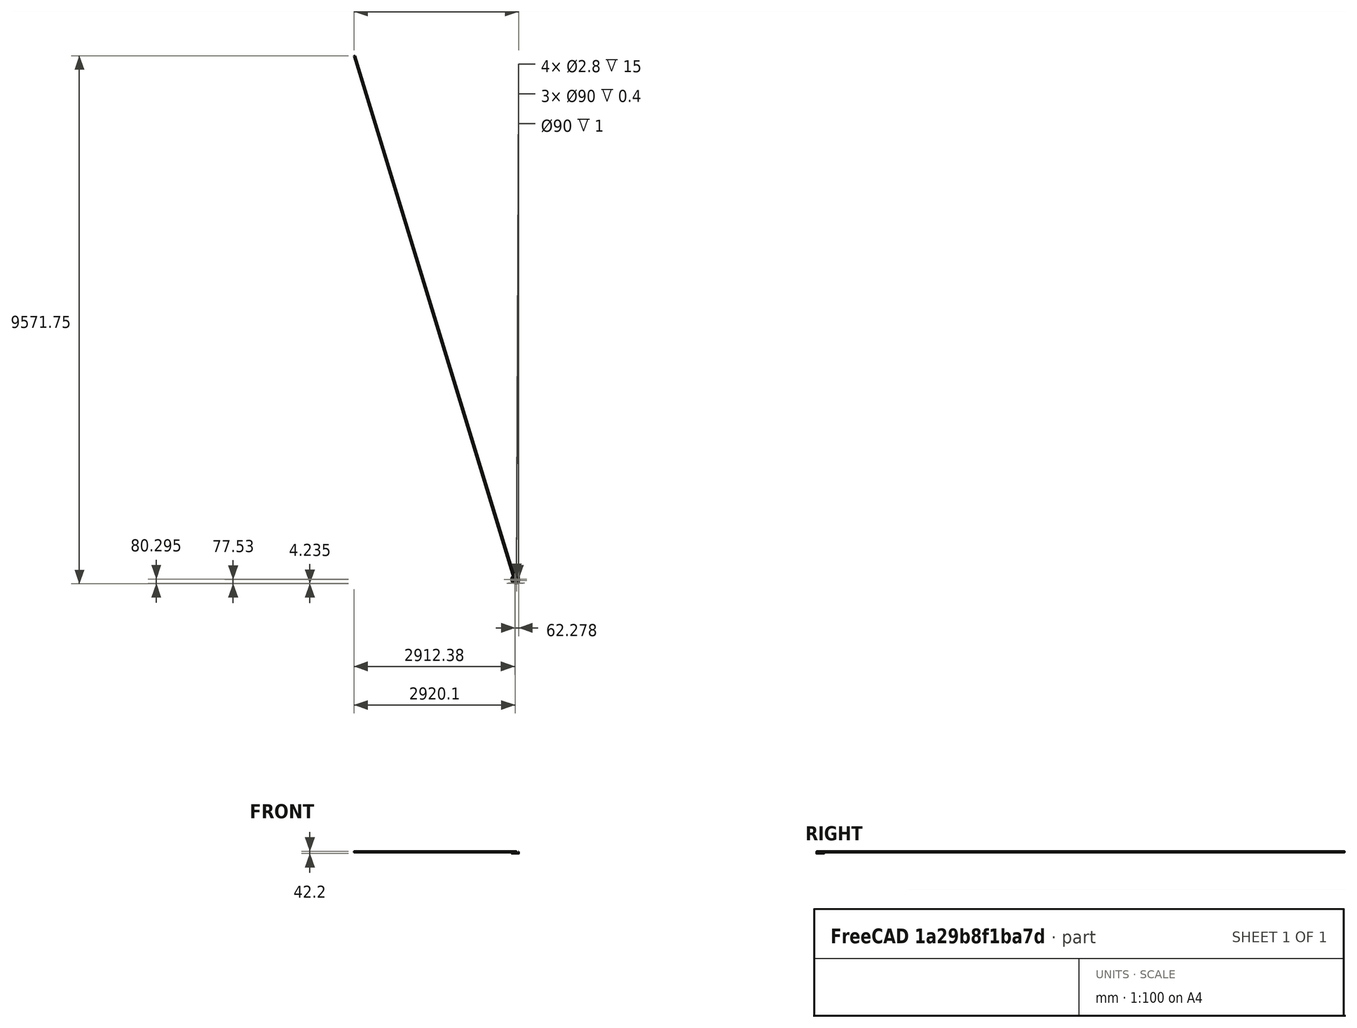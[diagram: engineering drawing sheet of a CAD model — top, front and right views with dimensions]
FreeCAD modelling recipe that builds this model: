
FCSTD DOCUMENT  (FreeCAD 0.16R)
Label: chainguard25TRev1.V5
License: All rights reserved
LicenseURL: http://en.wikipedia.org/wiki/All_rights_reserved
objects: Sketcher::SketchObject×9, PartDesign::Fillet×9, PartDesign::Pad×5, PartDesign::Pocket×4, Part::FeaturePython×3, Mesh::Feature×3
note: 39 computed .brp shape members not serialized (recipe doc carries the construction recipe); baked Part::Feature solids carry a one-line shape summary decoded from their .brp

FEATURE [Sketcher::SketchObject] Sketch001
  sketch-geometry (7):
    g0: LineSegment StartX=60 StartY=64 StartZ=0 EndX=0 EndY=64 EndZ=0
    g1: LineSegment StartX=60 StartY=-64 StartZ=0 EndX=0 EndY=-64 EndZ=0
    g2: ArcOfCircle CenterX=8.21903e-05 CenterY=0 CenterZ=0 NormalX=0 NormalY=0 NormalZ=1 Radius=64 StartAngle=1.5708 EndAngle=4.71239
    g3: Circle CenterX=0 CenterY=0 CenterZ=0 NormalX=0 NormalY=0 NormalZ=1 Radius=45
    g4: ArcOfCircle CenterX=60 CenterY=51 CenterZ=0 NormalX=0 NormalY=0 NormalZ=1 Radius=13 StartAngle=0 EndAngle=1.5708
    g5: ArcOfCircle CenterX=60 CenterY=-51 CenterZ=0 NormalX=0 NormalY=0 NormalZ=1 Radius=13 StartAngle=4.71239 EndAngle=6.28319
    g6: LineSegment StartX=73 StartY=51 StartZ=0 EndX=73 EndY=-51 EndZ=0
  constraints (23):
    c: Horizontal(g0)
    c: Horizontal(g1)
    c: Coincident(g2,g1)
    c: Coincident(g0,g2)
    c: DistanceX(g1,g0) = 0
    c: Equal(g0,g1)
    c: DistanceY(g1,g0) = 128
    c: Radius(g2) = 64
    c: Symmetric(g1,g0,g-1)
    c: Radius(g3) = 45
    c: Coincident(g3,g-1)
    c: PointOnObject(g4,g0)
    c: Radius(g4) = 13
    c: DistanceX(g0,g0) = 60
    c: Equal(g5,g4)
    c: Vertical(g6)
    c: DistanceX(g-1,g6) = 73
    c: Symmetric(g6,g6,g-1)
    c: DistanceY(g6,g6) = 102
    c: Coincident(g4,g6)
    c: Coincident(g5,g6)
    c: Coincident(g1,g5)
    c: Coincident(g0,g4)
FEATURE [PartDesign::Pad] Pad  label="Faceplate"
  Length = 1
  Length2 = 100
  Reversed = true
  Sketch = -> Sketch001
  Type = 0
FEATURE [Sketcher::SketchObject] Sketch002
  sketch-geometry (8):
    g0: LineSegment StartX=60 StartY=64 StartZ=0 EndX=0 EndY=64 EndZ=0
    g1: LineSegment StartX=60 StartY=-64 StartZ=0 EndX=0 EndY=-64 EndZ=0
    g2: ArcOfCircle CenterX=6.44712e-05 CenterY=0 CenterZ=0 NormalX=0 NormalY=0 NormalZ=1 Radius=64 StartAngle=1.5708 EndAngle=4.71239
    g3: LineSegment StartX=0 StartY=62 StartZ=0 EndX=60 EndY=62 EndZ=0
    g4: LineSegment StartX=0 StartY=-62 StartZ=0 EndX=60 EndY=-62 EndZ=0
    g5: LineSegment StartX=60 StartY=64 StartZ=0 EndX=60 EndY=62 EndZ=0
    g6: LineSegment StartX=60 StartY=-62 StartZ=0 EndX=60 EndY=-64 EndZ=0
    g7: ArcOfCircle CenterX=1.45954e-05 CenterY=0 CenterZ=0 NormalX=0 NormalY=0 NormalZ=1 Radius=62 StartAngle=1.5708 EndAngle=4.71239
  constraints (25):
    c: Horizontal(g0)
    c: Horizontal(g1)
    c: Coincident(g2,g1)
    c: Coincident(g0,g2)
    c: DistanceX(g1,g0) = 0
    c: Equal(g0,g1)
    c: DistanceY(g1,g0) = 128
    c: Radius(g2) = 64
    c: Symmetric(g1,g0,g-1)
    c: Radius(g7) = 62
    c: Parallel(g0,g3)
    c: DistanceY(g3,g0) = 2
    c: DistanceY(g1,g4) = 2
    c: Parallel(g4,g1)
    c: DistanceX(g0,g3) = 0
    c: DistanceX(g4) = 0
    c: DistanceX(g0) = 60
    c: Equal(g3,g0)
    c: Equal(g4,g0)
    c: Coincident(g4,g6)
    c: Coincident(g6,g1)
    c: Coincident(g5,g3)
    c: Coincident(g5,g0)
    c: Coincident(g7,g3)
    c: Coincident(g7,g4)
FEATURE [PartDesign::Pad] Pad001  label="Connector"
  Length = 10
  Length2 = 100
  Sketch = -> Sketch002
  Type = 0
FEATURE [Sketcher::SketchObject] Sketch004  label="BossST"
  sketch-geometry (5):
    g0: LineSegment StartX=41.8431 StartY=-62 StartZ=0 EndX=1.8431 EndY=-62 EndZ=0
    g1: LineSegment StartX=1.8431 StartY=-62 StartZ=0 EndX=1.8431 EndY=-75.5264 EndZ=0
    g2: LineSegment StartX=41.8431 StartY=-66 StartZ=0 EndX=41.8431 EndY=-62 EndZ=0
    g3: LineSegment StartX=4.42784 StartY=-77.439 StartZ=0 EndX=41.8431 EndY=-66 EndZ=0
    g4: ArcOfCircle CenterX=3.8431 CenterY=-75.5264 CenterZ=0 NormalX=0 NormalY=0 NormalZ=1 Radius=2 StartAngle=3.14159 EndAngle=5.00909
  constraints (14):
    c: Coincident(g0,g1)
    c: Vertical(g1)
    c: Vertical(g2)
    c: DistanceX(g0,g0) = 40
    c: Angle(g3) = 0.296706
    c: DistanceY(g0,g-1) = 62
    c: Horizontal(g0)
    c: DistanceY(g2,g2) = 4
    c: Coincident(g2,g0)
    c: Coincident(g3,g2)
    c: Tangent(g3,g4) = -1.5708
    c: Tangent(g1,g4) = -1.5708
    c: Radius(g4) = 2
    c: DistanceX(g-1,g0) = 1.8431
FEATURE [Sketcher::SketchObject] Sketch
  Support = -> Pad [Face8]
  sketch-geometry (4):
    g0: LineSegment StartX=65 StartY=35 StartZ=0 EndX=73 EndY=35 EndZ=0
    g1: LineSegment StartX=73 StartY=35 StartZ=0 EndX=73 EndY=-35 EndZ=0
    g2: LineSegment StartX=73 StartY=-35 StartZ=0 EndX=65 EndY=-35 EndZ=0
    g3: LineSegment StartX=65 StartY=-35 StartZ=0 EndX=65 EndY=35 EndZ=0
  constraints (12):
    c: Coincident(g0,g1)
    c: Coincident(g1,g2)
    c: Coincident(g2,g3)
    c: Coincident(g3,g0)
    c: Horizontal(g0)
    c: Horizontal(g2)
    c: Vertical(g1)
    c: Vertical(g3)
    c: Symmetric(g0,g2,g-1)
    c: DistanceX(g0,g0) = 8
    c: DistanceX(g-1,g0) = 73
    c: DistanceY(g3,g3) = 70
FEATURE [PartDesign::Pad] Pad003  label="SyncStiffener"
  Length = 3
  Length2 = 100
  Sketch = -> Sketch
  Type = 0
FEATURE [PartDesign::Pad] Pad005  label="ST Boss"
  Length = 31
  Length2 = 1
  Sketch = -> Sketch004
  Type = 4
FEATURE [Sketcher::SketchObject] Sketch005
  Placement = pos=(22.0436,-72.1013,0) rot=(0.978386,0.146221,0.146221;1.59265rad)
  Support = -> Pad005 [Face3]
  sketch-geometry (1):
    g0: Circle CenterX=0 CenterY=30 CenterZ=0 NormalX=0 NormalY=0 NormalZ=1 Radius=11.2
  constraints (3):
    c: Radius(g0) = 11.2
    c: DistanceY(g-1,g0) = 30
    c: PointOnObject(g0,g-2)
FEATURE [PartDesign::Pocket] Pocket  label="STHolePocket"
  Length = 5
  Sketch = -> Sketch005
  Type = 1
FEATURE [Sketcher::SketchObject] Sketch007
  Placement = pos=(0,0,31) rot=(0,0,1;0rad)
  Support = -> Pocket [Face4]
  sketch-geometry (4):
    g0: LineSegment StartX=-4.66376 StartY=-53.9533 StartZ=0 EndX=-5.90948 EndY=-71.4649 EndZ=0
    g1: LineSegment StartX=-5.90948 StartY=-71.4649 StartZ=0 EndX=38.1328 EndY=-58 EndZ=0
    g2: LineSegment StartX=38.1328 StartY=-58 StartZ=0 EndX=37.116 EndY=-54.0061 EndZ=0
    g3: LineSegment StartX=37.116 StartY=-54.0061 StartZ=0 EndX=-4.66376 EndY=-53.9533 EndZ=0
  constraints (12):
    c: Coincident(g0,g1)
    c: Coincident(g1,g2)
    c: Coincident(g2,g3)
    c: Coincident(g0,g3)
    c: Distance(g3) = 41.7798
    c: Distance(g0) = 17.5559
    c: Distance(g1) = 46.0546
    c: Distance(g2) = 4.12132
    c: DistanceX(g0,g-1) = 4.66376
    c: DistanceX(g0,g-1) = 5.90948
    c: DistanceY(g2,g-1) = 54.0061
    c: DistanceX(g1) = 38.1328
FEATURE [PartDesign::Pocket] Pocket006  label="STpocket1"
  Length = 22
  Sketch = -> Sketch007
  Type = 0
FEATURE [PartDesign::Fillet] Fillet  label="FaceFillet"
  Base = -> Pad003 [Edge4,Edge12,Edge20,Edge21,Edge22,Edge6,Edge23]
  Radius = 0.6
FEATURE [Sketcher::SketchObject] Sketch014
  ExternalGeometry = -> [Fillet]
  Placement = pos=(73,0,0) rot=(0.57735,0.57735,0.57735;2.0944rad)
  Support = -> Fillet [Face8]
  sketch-geometry (6):
    g0: LineSegment StartX=-35 StartY=3 StartZ=0 EndX=-24.5 EndY=31 EndZ=0
    g1: LineSegment StartX=-24.5 StartY=31 StartZ=0 EndX=-18.2 EndY=31 EndZ=0
    g2: LineSegment StartX=10.5 StartY=31 StartZ=0 EndX=35 EndY=3 EndZ=0
    g3: LineSegment StartX=35 StartY=3 StartZ=0 EndX=-35 EndY=3 EndZ=0
    g4: ArcOfCircle CenterX=-7 CenterY=31 CenterZ=0 NormalX=0 NormalY=0 NormalZ=1 Radius=11.2 StartAngle=3.14159 EndAngle=6.28319
    g5: LineSegment StartX=4.2 StartY=31 StartZ=0 EndX=10.5 EndY=31 EndZ=0
  constraints (16):
    c: Coincident(g0,g1)
    c: Coincident(g0,g3)
    c: Coincident(g1,g4)
    c: Coincident(g2,g3)
    c: Coincident(g2,g5)
    c: Coincident(g4,g5)
    c: Coincident(g0,g-4)
    c: Coincident(g-4,g2)
    c: DistanceX(g-1,g2) = 10.5
    c: DistanceY(g-1,g4) = 31
    c: Radius(g4) = 11.2
    c: DistanceX(g0,g2) = 35
    c: Symmetric(g2,g0,g4)
    c: Horizontal(g1)
    c: Horizontal(g5)
    c: DistanceY(g-1,g4) = 31
FEATURE [PartDesign::Pad] Pad006
  Length = 6
  Length2 = 100
  Reversed = true
  Sketch = -> Sketch014
  Type = 0
FEATURE [Sketcher::SketchObject] Sketch015
  ExternalGeometry = -> [Pad006]
  Placement = pos=(0,0,31) rot=(0,0,1;0rad)
  Support = -> Pad006 [Face7]
  sketch-geometry (2):
    g0: Circle CenterX=70 CenterY=7 CenterZ=0 NormalX=0 NormalY=0 NormalZ=1 Radius=1.4
    g1: Circle CenterX=70 CenterY=-21 CenterZ=0 NormalX=0 NormalY=0 NormalZ=1 Radius=1.4
  constraints (6):
    c: Radius(g1) = 1.4
    c: Equal(g1,g0)
    c: Distance(g1,g0) = 28
    c: Distance(g0,g-3) = 2.8
    c: Distance(g1,g-6) = 3
    c: Distance(g0,g-4) = 3
FEATURE [PartDesign::Pocket] Pocket008  label="SyncHoles"
  Length = 15
  Sketch = -> Sketch015
  Type = 0
FEATURE [Sketcher::SketchObject] Sketch016
  ExternalGeometry = -> [Pocket006]
  Placement = pos=(0,0,31) rot=(0,0,1;0rad)
  Support = -> Pocket006 [Face12]
  sketch-geometry (2):
    g0: Circle CenterX=34.4985 CenterY=-65.1084 CenterZ=0 NormalX=0 NormalY=0 NormalZ=1 Radius=1.4
    g1: Circle CenterX=7.72201 CenterY=-73.2948 CenterZ=0 NormalX=0 NormalY=0 NormalZ=1 Radius=1.4
  constraints (6):
    c: Radius(g1) = 1.4
    c: Equal(g1,g0)
    c: Distance(g0,g1) = 28
    c: Distance(g0,g-4) = 2.8
    c: Distance(g0,g-6) = 3
    c: Distance(g1,g-5) = 3
FEATURE [PartDesign::Fillet] Fillet001  label="ConnectorFillet1"
  Base = -> Pad001 [Edge13,Edge24]
  Radius = 6
FEATURE [PartDesign::Fillet] Fillet002  label="ConnectorFillet"
  Base = -> Fillet001 [Edge4]
  Radius = 1
FEATURE [PartDesign::Pocket] Pocket009  label="STholes"
  Length = 15
  Sketch = -> Sketch016
  Type = 0
FEATURE [PartDesign::Fillet] Fillet003
  Base = -> Pocket009 [Edge11]
  Radius = 2.5
FEATURE [PartDesign::Fillet] Fillet004
  Base = -> Fillet003 [Edge15]
  Radius = 1
FEATURE [PartDesign::Fillet] Fillet005
  Base = -> Fillet004 [Edge4]
  Radius = 1
FEATURE [PartDesign::Fillet] Fillet006
  Base = -> Fillet005 [Edge30]
  Radius = 1
FEATURE [PartDesign::Fillet] Fillet007
  Base = -> Fillet006 [Edge20]
  Radius = 0.5
FEATURE [PartDesign::Fillet] Fillet008
  Base = -> Pocket008 [Edge10,Edge14,Edge8,Edge7]
  Radius = 1
FEATURE [Part::FeaturePython] refine  label="refine_ConnectorFillet"  # WARN: FeaturePython — macro-defined, semantics opaque (R4)
  Base = -> Fillet002
FEATURE [Part::FeaturePython] refine001  label="refine_Fillet007"  # WARN: FeaturePython — macro-defined, semantics opaque (R4)
  Base = -> Fillet007
FEATURE [Part::FeaturePython] refine002  label="refine_Fillet008"  # WARN: FeaturePython — macro-defined, semantics opaque (R4)
  Base = -> Fillet008
FEATURE [Mesh::Feature] Mesh  label="refine_ConnectorFillet (Meshed)"
FEATURE [Mesh::Feature] Mesh001  label="refine_Fillet007 (Meshed)"
FEATURE [Mesh::Feature] Mesh002  label="refine_Fillet008 (Meshed)"
